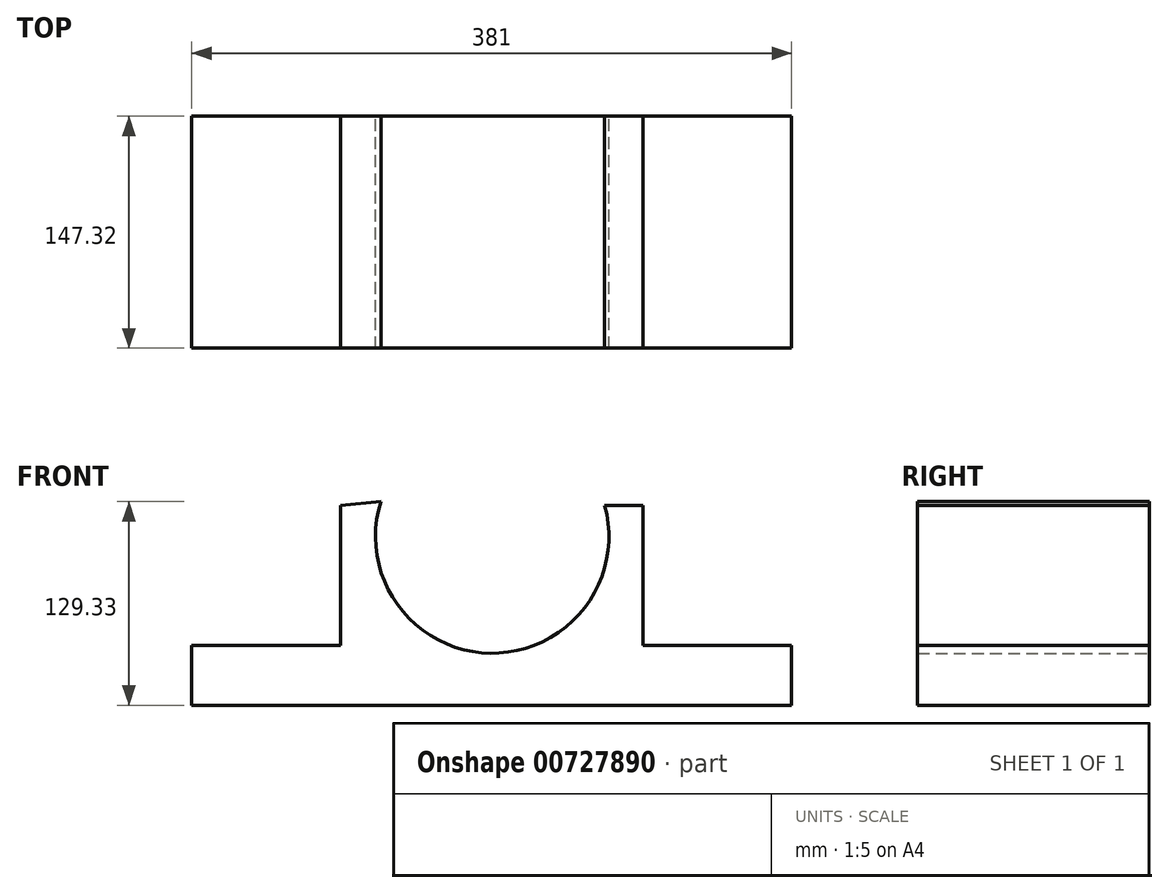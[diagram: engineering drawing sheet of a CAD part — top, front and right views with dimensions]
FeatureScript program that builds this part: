
annotation { "Feature Type Name" : "Feature", "Feature Type Description" : "" }
export const myFeature = defineFeature(function(context is Context, id is Id, definition is map)
    precondition{}
    {
        {
            var Q0;
            Q0=qCreatedBy(makeId("Front.planeOp"),FACE);
            var sketch = newSketch(context, id + "F0", { "sketchPlane" : qUnion([Q0])});
            skLineSegment(sketch, "E0", {"start": v(-227.23, 0) * mm, "end": v(153.77, 0) * mm});
            skLineSegment(sketch, "E1", {"start": v(-227.23, 0) * mm, "end": v(-227.23, 38.1) * mm});
            skLineSegment(sketch, "E2", {"start": v(153.77, 0) * mm, "end": v(153.77, 38.1) * mm});
            skLineSegment(sketch, "E3", {"start": v(-227.23, 38.1) * mm, "end": v(-132.74, 38.1) * mm});
            skLineSegment(sketch, "E4", {"start": v(153.77, 38.1) * mm, "end": v(59.28, 38.1) * mm});
            skLineSegment(sketch, "E5", {"start": v(-132.74, 38.1) * mm, "end": v(-132.74, 127) * mm});
            skLineSegment(sketch, "E6", {"start": v(59.28, 38.1) * mm, "end": v(59.28, 127) * mm});
            skArc(sketch, "E7", {"start": v(-107.19, 129.33) * mm, "mid": v(-37.64, 33.08) * mm, "end": v(34.96, 127.03) * mm});
            skLineSegment(sketch, "E8", {"start": v(-132.74, 127) * mm, "end": v(-107.19, 129.33) * mm});
            skLineSegment(sketch, "E9", {"start": v(34.96, 127.03) * mm, "end": v(59.28, 127) * mm});
            skSolve(sketch);
        }
        {
            var Q0;
            Q0=makeQuery(id+"F0.imprint","IMPRINT",FACE,{"disambiguationData":[TD([[makeQuery(id+"F0.imprint","IMPRINT",EDGE,{"derivedFrom":sQuery(id+"F0.wireOp",EDGE,"E0")}),1.0]])]});
            extrude(context, id + "F1", {"entities" : qUnion([Q0]), "depth" : 147.32 * mm, "offsetDistance" : 25.4 * mm});
        }
    });
